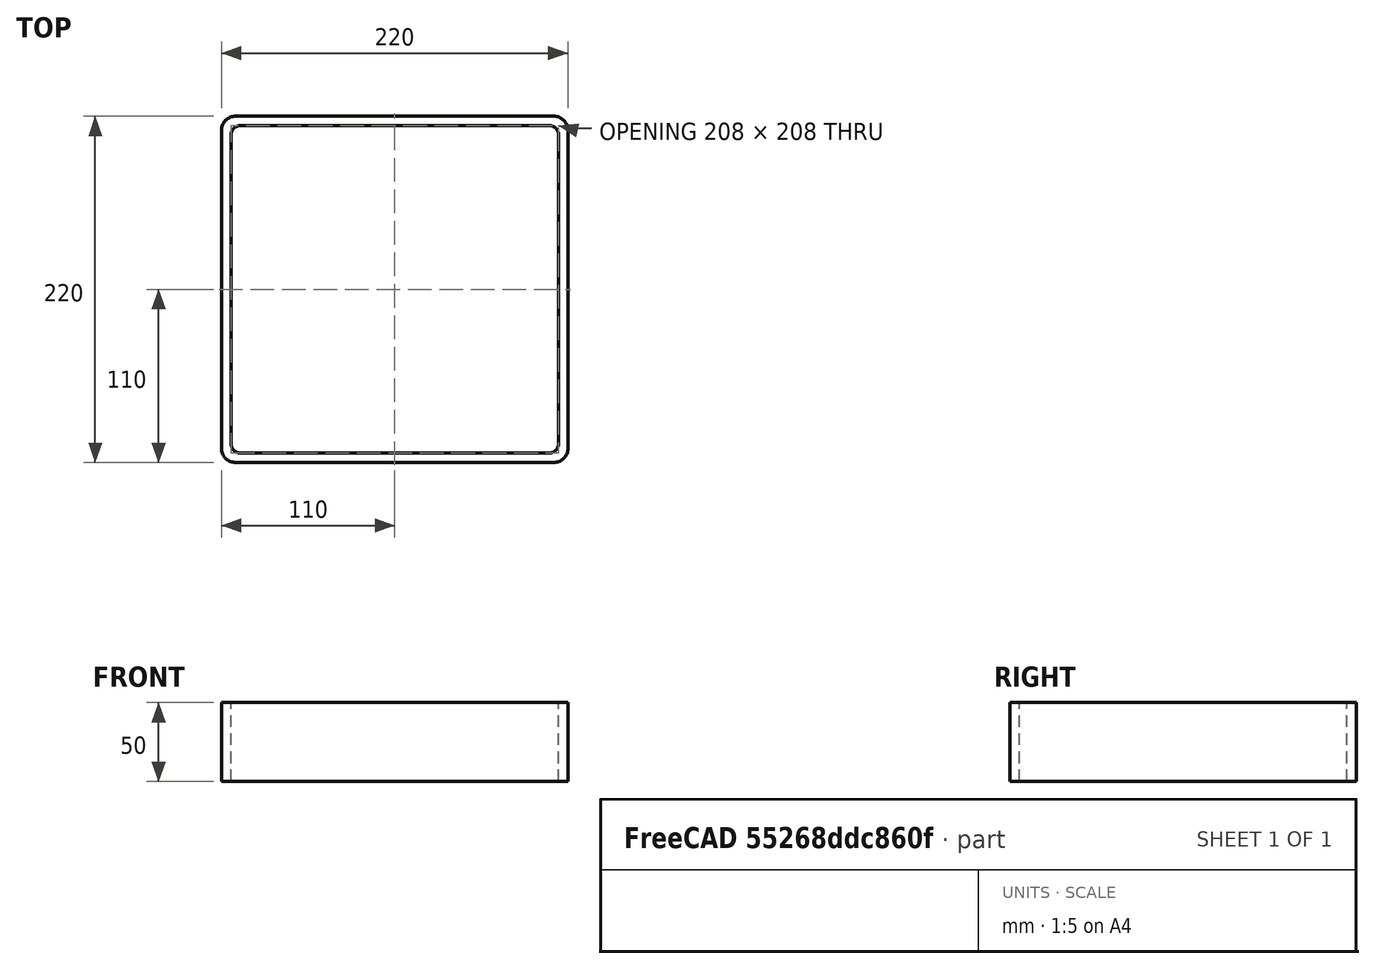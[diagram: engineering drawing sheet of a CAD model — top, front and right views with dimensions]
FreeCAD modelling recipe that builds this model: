
FCSTD DOCUMENT  (FreeCAD 0.15R4671 (Git))
Label: Square hollow section 220x220x6 EN10219 S235JRH
License: All rights reserved
LicenseURL: http://en.wikipedia.org/wiki/All_rights_reserved
objects: Sketcher::SketchObject×1, Part::Extrusion×1
note: 2 computed .brp shape members not serialized (recipe doc carries the construction recipe); baked Part::Feature solids carry a one-line shape summary decoded from their .brp

FEATURE [Sketcher::SketchObject] Sketch
  sketch-geometry (16):
    g0: LineSegment StartX=-98 StartY=104 StartZ=0 EndX=98 EndY=104 EndZ=0
    g1: LineSegment StartX=104 StartY=98 StartZ=0 EndX=104 EndY=-98 EndZ=0
    g2: LineSegment StartX=98 StartY=-104 StartZ=0 EndX=-98 EndY=-104 EndZ=0
    g3: LineSegment StartX=-104 StartY=-98 StartZ=0 EndX=-104 EndY=98 EndZ=0
    g4: LineSegment StartX=-101 StartY=110 StartZ=0 EndX=101 EndY=110 EndZ=0
    g5: LineSegment StartX=110 StartY=101 StartZ=0 EndX=110 EndY=-101 EndZ=0
    g6: LineSegment StartX=101 StartY=-110 StartZ=0 EndX=-101 EndY=-110 EndZ=0
    g7: LineSegment StartX=-110 StartY=-101 StartZ=0 EndX=-110 EndY=101 EndZ=0
    g8: ArcOfCircle CenterX=-98 CenterY=98 CenterZ=0 NormalX=0 NormalY=0 NormalZ=1 Radius=6 StartAngle=1.5708 EndAngle=3.14159
    g9: ArcOfCircle CenterX=98 CenterY=98 CenterZ=0 NormalX=0 NormalY=0 NormalZ=1 Radius=6 StartAngle=0 EndAngle=1.5708
    g10: ArcOfCircle CenterX=98 CenterY=-98 CenterZ=0 NormalX=0 NormalY=0 NormalZ=1 Radius=6 StartAngle=4.71239 EndAngle=6.28319
    g11: ArcOfCircle CenterX=-98 CenterY=-98 CenterZ=0 NormalX=0 NormalY=0 NormalZ=1 Radius=6 StartAngle=3.14159 EndAngle=4.71239
    g12: ArcOfCircle CenterX=101 CenterY=101 CenterZ=0 NormalX=0 NormalY=0 NormalZ=1 Radius=9 StartAngle=0 EndAngle=1.5708
    g13: ArcOfCircle CenterX=101 CenterY=-101 CenterZ=0 NormalX=0 NormalY=0 NormalZ=1 Radius=9 StartAngle=4.71239 EndAngle=6.28319
    g14: ArcOfCircle CenterX=-101 CenterY=-101 CenterZ=0 NormalX=0 NormalY=0 NormalZ=1 Radius=9 StartAngle=3.14159 EndAngle=4.71239
    g15: ArcOfCircle CenterX=-101 CenterY=101 CenterZ=0 NormalX=0 NormalY=0 NormalZ=1 Radius=9 StartAngle=1.5708 EndAngle=3.14159
  constraints (36):
    c: Horizontal(g2)
    c: Vertical(g3)
    c: Horizontal(g6)
    c: Vertical(g7)
    c: Tangent(g3,g8) = 1.5708
    c: Tangent(g0,g8) = 1.5708
    c: Tangent(g0,g9) = 1.5708
    c: Tangent(g1,g9) = 1.5708
    c: Tangent(g1,g10) = 1.5708
    c: Tangent(g2,g10) = 1.5708
    c: Tangent(g2,g11) = 1.5708
    c: Tangent(g3,g11) = 1.5708
    c: Tangent(g4,g12) = 1.5708
    c: Tangent(g5,g12) = 1.5708
    c: Tangent(g5,g13) = 1.5708
    c: Tangent(g6,g13) = 1.5708
    c: Tangent(g6,g14) = 1.5708
    c: Tangent(g7,g14) = 1.5708
    c: Tangent(g7,g15) = 1.5708
    c: Tangent(g4,g15) = 1.5708
    c: Equal(g9,g8)
    c: Equal(g9,g11)
    c: Equal(g9,g10)
    c: Equal(g12,g15)
    c: Equal(g12,g14)
    c: Equal(g12,g13)
    c: Symmetric(g4,g6,g-1)
    c: Symmetric(g7,g5,g-2)
    c: DistanceY(g4,g6) = -220
    c: DistanceX(g7,g5) = 220
    c: Symmetric(g3,g1,g-2)
    c: Symmetric(g0,g2,g-1)
    c: DistanceY(g0,g4) = 6
    c: DistanceX(g5,g1) = -6
    c: Radius(g9) = 6
    c: Radius(g12) = 9
FEATURE [Part::Extrusion] Extrude  label="Square hollow section 220x220x6 EN10219 S235JRH"
  Base = -> Sketch
  Dir = (0,0,50)
  Solid = true
